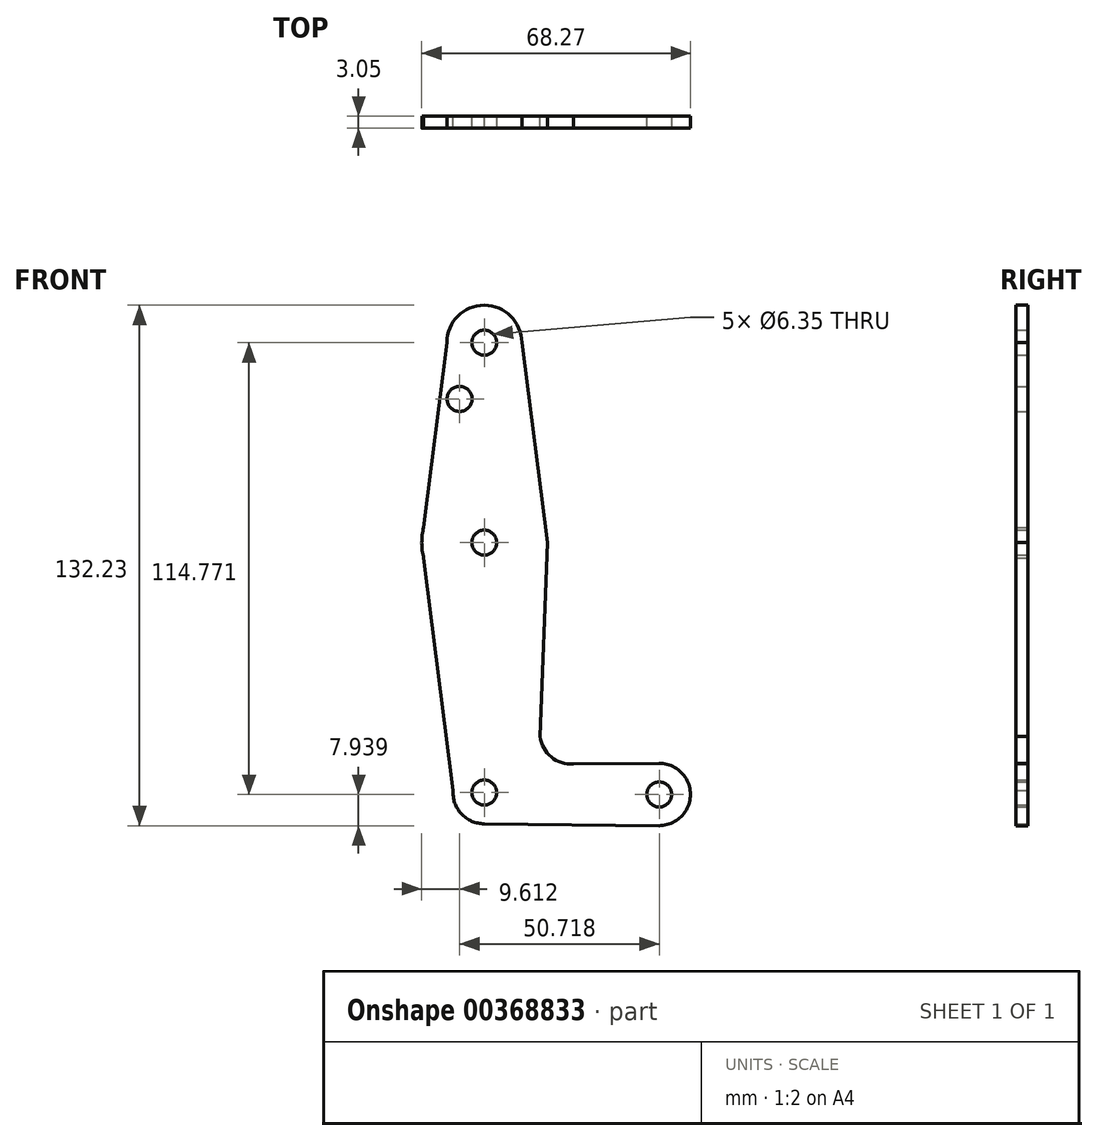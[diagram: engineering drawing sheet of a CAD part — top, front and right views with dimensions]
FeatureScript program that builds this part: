
annotation { "Feature Type Name" : "Feature", "Feature Type Description" : "" }
export const myFeature = defineFeature(function(context is Context, id is Id, definition is map)
    precondition{}
    {
        {
            var Q0;
            Q0=qCreatedBy(makeId("Front.planeOp"),FACE);
            var sketch = newSketch(context, id + "F0", { "sketchPlane" : qUnion([Q0])});
            skCircle(sketch, "E0", {"center": v(0, 50.8) * mm, "radius": 9.53 * mm});
            skCircle(sketch, "E1", {"center": v(0, 0) * mm, "radius": 15.88 * mm});
            skCircle(sketch, "E2", {"center": v(0, -63.5) * mm, "radius": 7.94 * mm});
            skCircle(sketch, "E3", {"center": v(44.45, -63.97) * mm, "radius": 7.94 * mm});
            skCircle(sketch, "E4", {"center": v(0, -63.5) * mm, "radius": 3.18 * mm});
            skCircle(sketch, "E5", {"center": v(0, 0) * mm, "radius": 3.18 * mm});
            skCircle(sketch, "E6", {"center": v(0, 50.8) * mm, "radius": 3.18 * mm});
            skCircle(sketch, "E7", {"center": v(44.45, -63.97) * mm, "radius": 3.18 * mm});
            skCircle(sketch, "E8", {"center": v(-6.27, 36.53) * mm, "radius": 3.18 * mm});
            skLineSegment(sketch, "E9", {"start": v(-9.52, 50.87) * mm, "end": v(-15.88, 0) * mm});
            skLineSegment(sketch, "E10", {"start": v(-15.87, 0) * mm, "end": v(-7.91, -62.9) * mm});
            skLineSegment(sketch, "E11", {"start": v(9.52, 50.87) * mm, "end": v(16, 0) * mm});
            skLineSegment(sketch, "E12", {"start": v(0, -71.44) * mm, "end": v(44.37, -71.9) * mm});
            skLineSegment(sketch, "E13", {"start": v(44.37, -56.03) * mm, "end": v(22.69, -56.26) * mm});
            skArc(sketch, "E14", {"start": v(14.2, -49.22) * mm, "mid": v(17.02, -54.46) * mm, "end": v(22.69, -56.26) * mm});
            skLineSegment(sketch, "E15", {"start": v(16, 0) * mm, "end": v(14.2, -49.22) * mm});
            skSolve(sketch);
        }
        {
            var Q0;
            Q0 = qSketchRegion(id + "F0", true);
            extrude(context, id + "F1", {"entities" : qUnion([Q0]), "depth" : 3.05 * mm});
        }
    });
